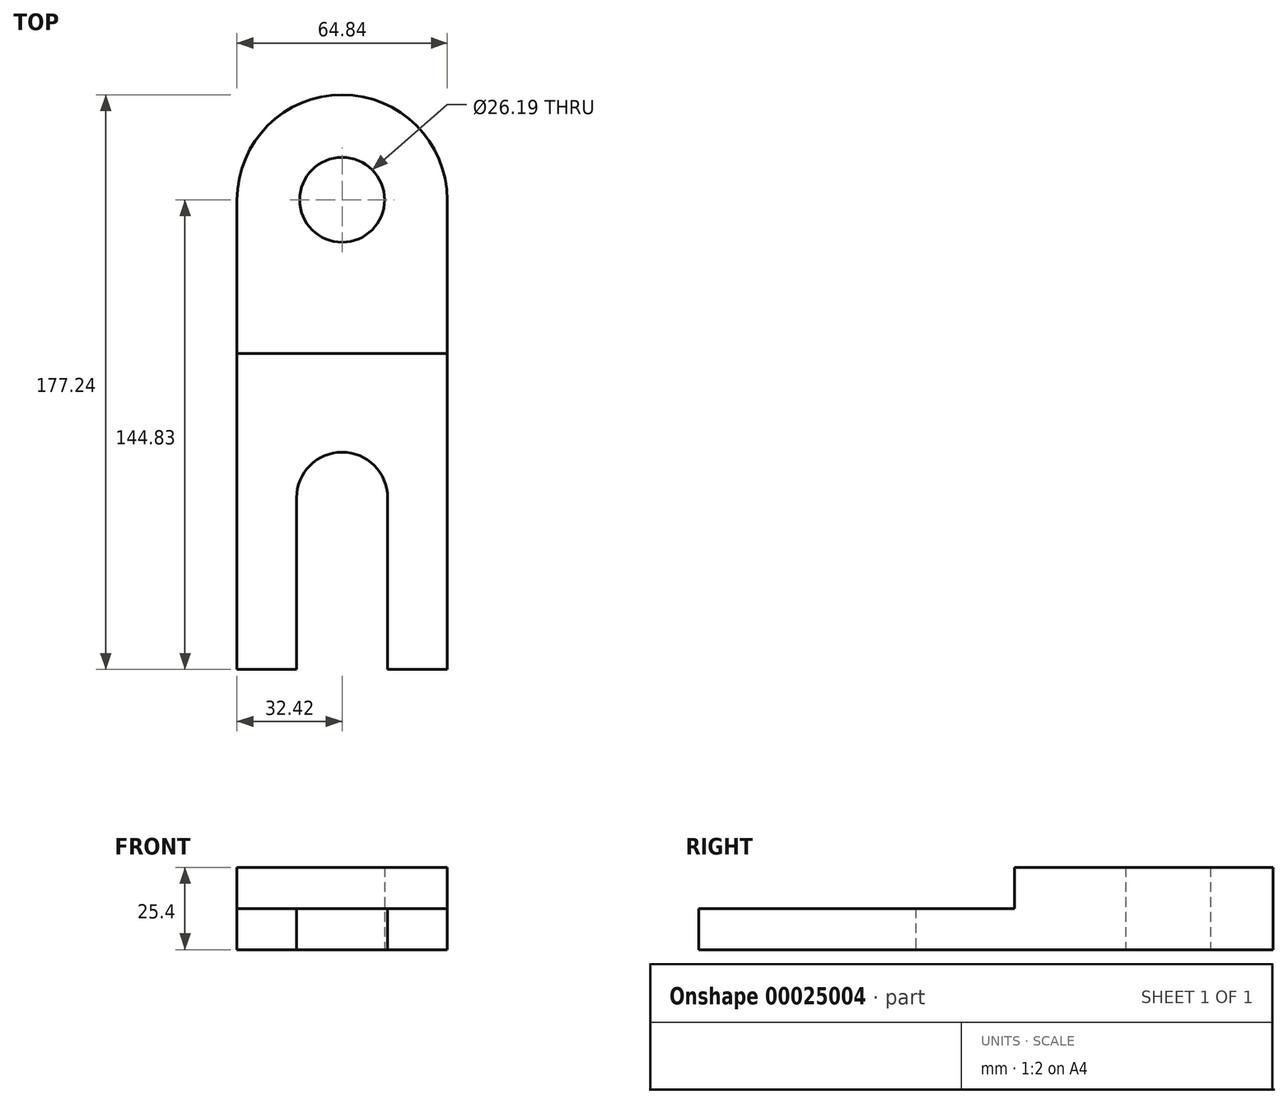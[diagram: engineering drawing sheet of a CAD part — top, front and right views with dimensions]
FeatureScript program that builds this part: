
annotation { "Feature Type Name" : "Feature", "Feature Type Description" : "" }
export const myFeature = defineFeature(function(context is Context, id is Id, definition is map)
    precondition{}
    {
        {
            var Q0;
            Q0=qCreatedBy(makeId("Top.planeOp"),FACE);
            var sketch = newSketch(context, id + "F0", { "sketchPlane" : qUnion([Q0])});
            skLineSegment(sketch, "E0.rect.top", {"start": v(-32.42, -88.62) * mm, "end": v(-14.03, -88.62) * mm});
            skLineSegment(sketch, "E0.rect.left", {"start": v(-32.42, 56.2) * mm, "end": v(-32.42, -88.62) * mm});
            skLineSegment(sketch, "E0.rect.right", {"start": v(32.42, 56.2) * mm, "end": v(32.42, -88.62) * mm});
            skPoint(sketch, "E0.rect.middle", {"position": v(0, 0) * mm});
            skArc(sketch, "E1", {"start": v(32.42, 56.2) * mm, "mid": v(0, 88.62) * mm, "end": v(-32.42, 56.2) * mm});
            skPoint(sketch, "E2.orphan", {"position": v(-32.42, 88.62) * mm});
            skPoint(sketch, "E3.orphan", {"position": v(32.42, 88.62) * mm});
            skCircle(sketch, "E4", {"center": v(0, 56.2) * mm, "radius": 13.1 * mm});
            skLineSegment(sketch, "E5.left", {"start": v(-14.03, -88.62) * mm, "end": v(-14.03, -35.63) * mm});
            skLineSegment(sketch, "E5.right", {"start": v(14.03, -88.62) * mm, "end": v(14.03, -35.63) * mm});
            skArc(sketch, "E6", {"start": v(14.03, -35.63) * mm, "mid": v(0, -21.6) * mm, "end": v(-14.03, -35.63) * mm});
            skLineSegment(sketch, "E7.trimOffspring", {"start": v(14.03, -88.62) * mm, "end": v(32.42, -88.62) * mm});
            skLineSegment(sketch, "E8", {"start": v(-32.42, 8.81) * mm, "end": v(32.42, 8.81) * mm});
            skSolve(sketch);
        }
        {
            var Q0;
            Q0 = qSketchRegion(id + "F0", true);
            extrude(context, id + "F1", {"entities" : qUnion([Q0]), "depth" : 12.7 * mm});
        }
        {
            var Q0;
            {var subQ1=sQuery(id+"F0.wireOp",EDGE,"E1");Q0=makeQuery(id+"F0.imprint","IMPRINT",FACE,{"disambiguationData":[TD([[makeQuery(id+"F0.imprint","IMPRINT",EDGE,{"derivedFrom":subQ1}),1.0]])]});}
            extrude(context, id + "F2", {"entities" : qUnion([Q0]), "operationType" : NewBodyOperationType.ADD, "depth" : 25.4 * mm});
        }
    });
